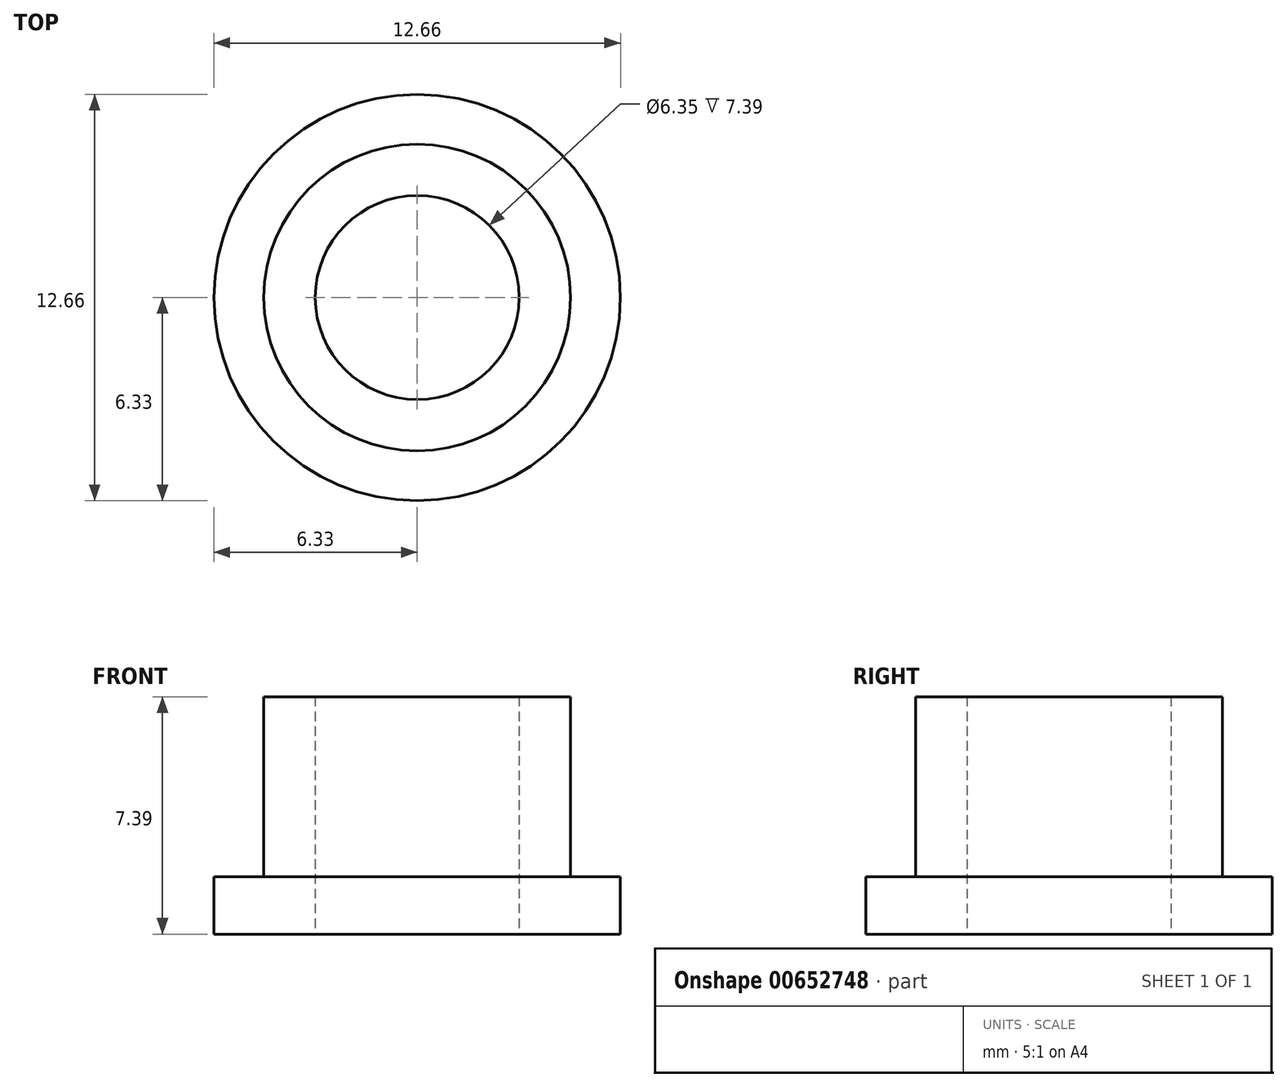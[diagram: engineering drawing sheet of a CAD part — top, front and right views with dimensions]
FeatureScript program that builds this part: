
annotation { "Feature Type Name" : "Feature", "Feature Type Description" : "" }
export const myFeature = defineFeature(function(context is Context, id is Id, definition is map)
    precondition{}
    {
        {
            var Q0;
            Q0=qCreatedBy(makeId("Top.planeOp"),FACE);
            var sketch = newSketch(context, id + "F0", { "sketchPlane" : qUnion([Q0])});
            skCircle(sketch, "E0", {"center": v(0, 0) * mm, "radius": 6.32 * mm});
            skSolve(sketch);
        }
        {
            var Q0;
            Q0=qCreatedBy(makeId("Top.planeOp"),FACE);
            var sketch = newSketch(context, id + "F1", { "sketchPlane" : qUnion([Q0])});
            skCircle(sketch, "E1", {"center": v(0, 0) * mm, "radius": 4.78 * mm});
            skSolve(sketch);
        }
        {
            var Q0;
            Q0=makeQuery(id+"F0.imprint","IMPRINT",FACE,{"disambiguationData":[TD([[makeQuery(id+"F0.imprint","IMPRINT",EDGE,{"derivedFrom":sQuery(id+"F0.wireOp",EDGE,"E0")}),1.0]])]});
            var Q1;
            Q1=sQuery(id+"F0.wireOp",EDGE,"E0");
            var Q2;
            Q2=sQuery(id+"F1.wireOp",EDGE,"E1");
            extrude(context, id + "F2", {"entities" : qUnion([Q0]), "surfaceEntities" : qUnion([Q1, Q2]), "depth" : 1.79 * mm, "offsetDistance" : 25.4 * mm});
        }
        {
            var Q0;
            Q0 = qSketchRegion(id + "F1", true);
            extrude(context, id + "F3", {"entities" : qUnion([Q0]), "operationType" : NewBodyOperationType.ADD, "depth" : 7.39 * mm, "offsetDistance" : 25.4 * mm});
        }
        {
            var Q0;
            Q0=qCreatedBy(makeId("Top.planeOp"),FACE);
            var sketch = newSketch(context, id + "F4", { "sketchPlane" : qUnion([Q0])});
            skCircle(sketch, "E2", {"center": v(0, 0) * mm, "radius": 3.65 * mm});
            skSolve(sketch);
        }
        {
            var Q0;
            Q0=sQuery(id+"F4.wireOp",VERTEX,"E2.center");
            var Q1;
            Q1=makeQuery(id+"F2.opExtrude","SWEPT_BODY",BODY,{"disambiguationData":[OSD([sQuery(id+"F0.wireOp",EDGE,"E0")])]});
            hole(context, id + "F5", {"style" : HoleStyle.SIMPLE, "endStyle" : HoleEndStyle.THROUGH, "oppositeDirection" : true, "holeDiameter" : 6.35 * mm, "majorDiameter" : 6.35 * mm, "isTappedThrough" : true, "tappedDepth" : 12.7 * mm, "tapClearance" : 3, "locations" : qUnion([Q0]), "scope" : qUnion([Q1])});
        }
    });
